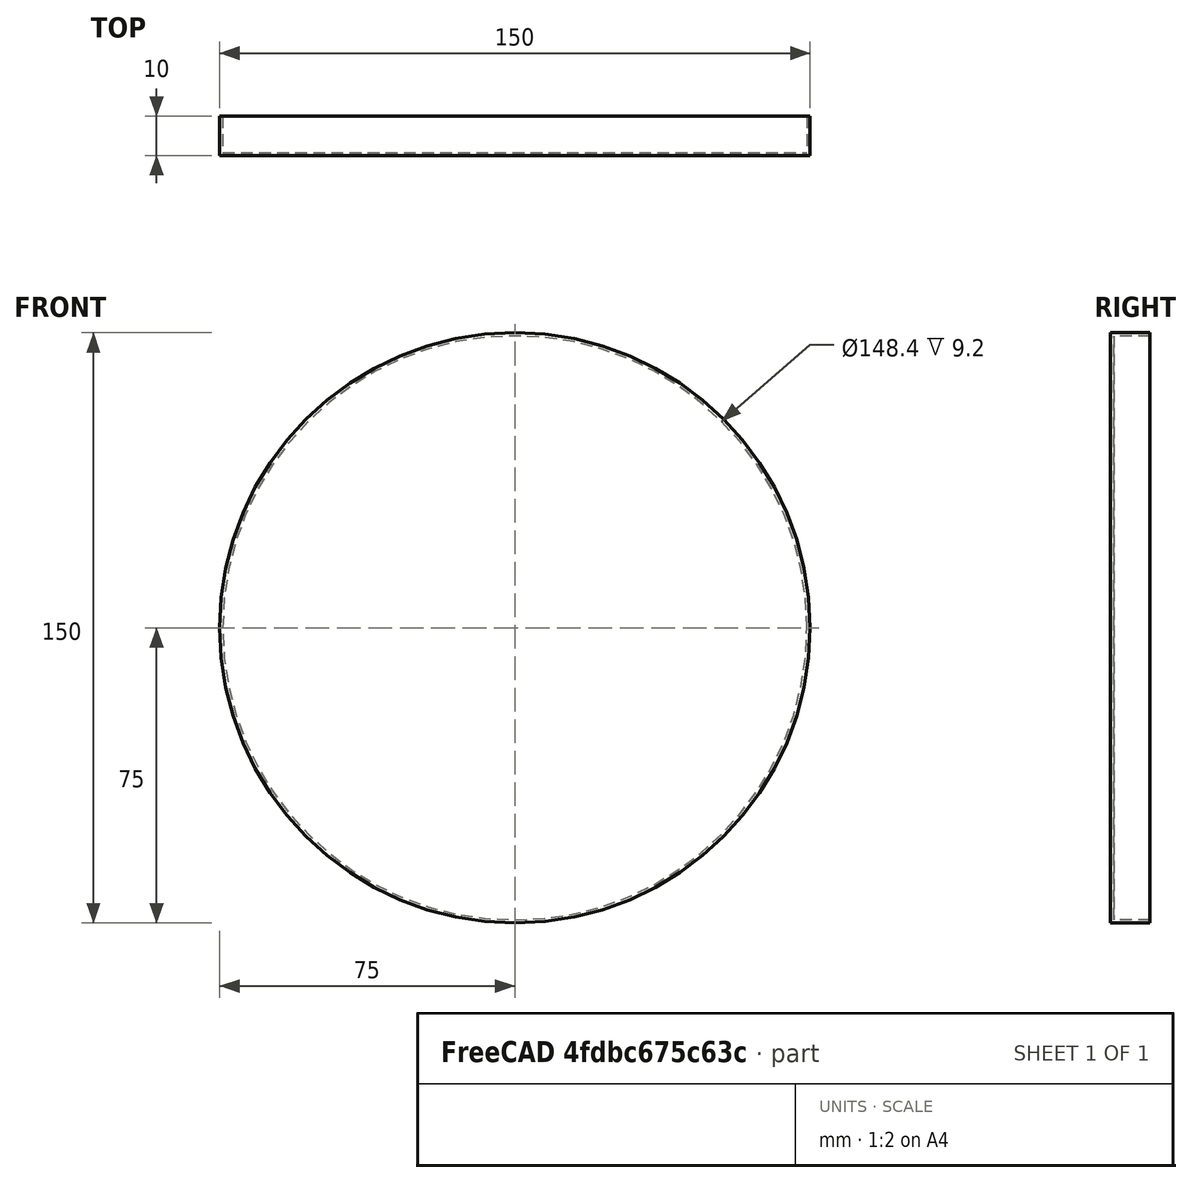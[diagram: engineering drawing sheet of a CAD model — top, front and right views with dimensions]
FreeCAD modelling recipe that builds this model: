
FCSTD DOCUMENT  (FreeCAD 0.19R24366 (Git))
Label: 18 cm dia plate
License: All rights reserved
LicenseURL: http://en.wikipedia.org/wiki/All_rights_reserved
objects: Sketcher::SketchObject×1, PartDesign::Revolution×1, PartDesign::Body×1
note: 4 computed .brp shape members not serialized (recipe doc carries the construction recipe); baked Part::Feature solids carry a one-line shape summary decoded from their .brp

FEATURE [Sketcher::SketchObject] Sketch
  FullyConstrained = true
  MapMode = 5
  Support = -> [XY_Plane]
  sketch-geometry (6):
    g0: LineSegment StartX=0 StartY=0 StartZ=0 EndX=-75 EndY=0 EndZ=0
    g1: LineSegment StartX=-75 StartY=0 StartZ=0 EndX=-75 EndY=10 EndZ=0
    g2: LineSegment StartX=-75 StartY=10 StartZ=0 EndX=-74.2 EndY=10 EndZ=0
    g3: LineSegment StartX=-74.2 StartY=10 StartZ=0 EndX=-74.2 EndY=0.8 EndZ=0
    g4: LineSegment StartX=-74.2 StartY=0.8 StartZ=0 EndX=0 EndY=0.8 EndZ=0
    g5: LineSegment StartX=0 StartY=0.8 StartZ=0 EndX=0 EndY=0 EndZ=0
  constraints (17):
    c: Coincident(g-1,g0)
    c: PointOnObject(g0,g-1)
    c: Coincident(g0,g1)
    c: Coincident(g1,g2)
    c: Horizontal(g2)
    c: Coincident(g2,g3)
    c: Coincident(g3,g4)
    c: PointOnObject(g4,g-2)
    c: Horizontal(g4)
    c: Coincident(g4,g5)
    c: Coincident(g5,g0)
    c: Vertical(g3)
    c: Vertical(g1)
    c: DistanceX(g2,g2) = 0.8
    c: DistanceY(g5,g5) = 0.8
    c: DistanceX(g0,g0) = 75
    c: DistanceY(g1,g1) = 10
FEATURE [PartDesign::Revolution] Revolution
  Angle = 360
  Axis = (0,1,0)
  Base = (0,0,0)
  Profile = -> Sketch
  ReferenceAxis = -> Sketch [V_Axis]
FEATURE [PartDesign::Body] Body
  Group = -> [Sketch,Revolution]
  Origin = -> Origin
  Tip = -> Revolution
